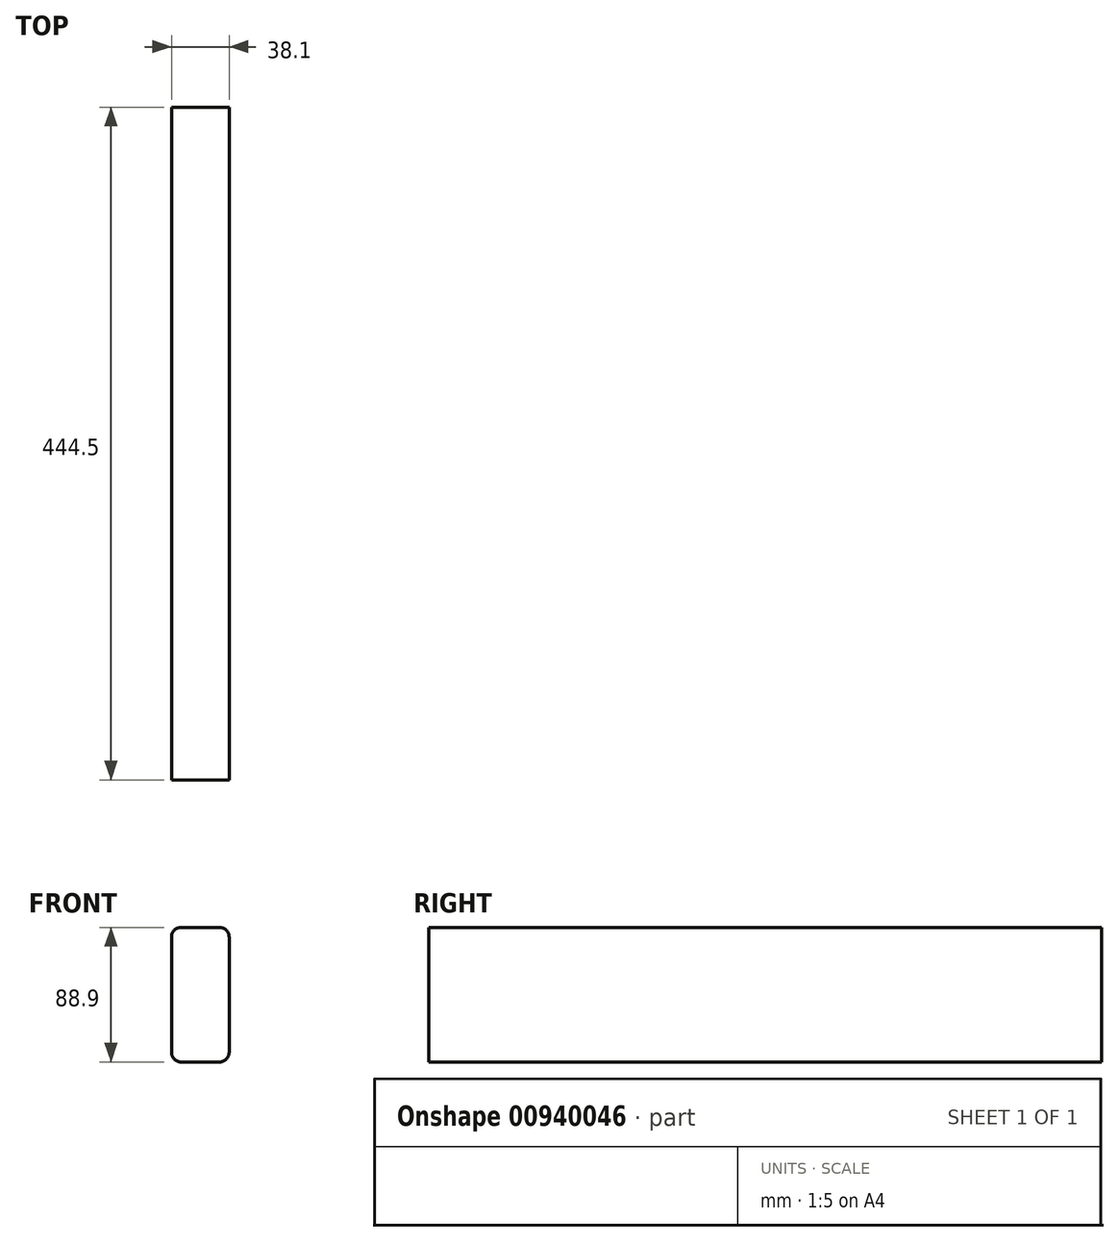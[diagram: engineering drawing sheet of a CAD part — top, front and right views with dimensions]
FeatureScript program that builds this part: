
annotation { "Feature Type Name" : "Feature", "Feature Type Description" : "" }
export const myFeature = defineFeature(function(context is Context, id is Id, definition is map)
    precondition{}
    {
        {
            var Q0;
            Q0=qCreatedBy(makeId("Front.planeOp"),FACE);
            var sketch = newSketch(context, id + "F0", { "sketchPlane" : qUnion([Q0])});
            skLineSegment(sketch, "E0.bottom", {"start": v(12.7, 44.45) * mm, "end": v(-12.7, 44.45) * mm});
            skLineSegment(sketch, "E0.top", {"start": v(12.7, -44.45) * mm, "end": v(-12.7, -44.45) * mm});
            skLineSegment(sketch, "E0.left", {"start": v(19.05, 38.1) * mm, "end": v(19.05, -38.1) * mm});
            skLineSegment(sketch, "E0.right", {"start": v(-19.05, 38.1) * mm, "end": v(-19.05, -38.1) * mm});
            skPoint(sketch, "E0.middle", {"position": v(0, 0) * mm});
            skPoint(sketch, "E1.visualSharp", {"position": v(-19.05, 44.45) * mm});
            skArc(sketch, "E1.filletArc", {"start": v(-12.7, 44.45) * mm, "mid": v(-17.2, 42.6) * mm, "end": v(-19.05, 38.1) * mm});
            skPoint(sketch, "E2.visualSharp", {"position": v(19.05, 44.45) * mm});
            skArc(sketch, "E2.filletArc", {"start": v(19.05, 38.1) * mm, "mid": v(17.2, 42.6) * mm, "end": v(12.7, 44.45) * mm});
            skPoint(sketch, "E3.visualSharp", {"position": v(19.05, -44.45) * mm});
            skArc(sketch, "E3.filletArc", {"start": v(12.7, -44.45) * mm, "mid": v(17.2, -42.6) * mm, "end": v(19.05, -38.1) * mm});
            skPoint(sketch, "E4.visualSharp", {"position": v(-19.05, -44.45) * mm});
            skArc(sketch, "E4.filletArc", {"start": v(-19.05, -38.1) * mm, "mid": v(-17.2, -42.6) * mm, "end": v(-12.7, -44.45) * mm});
            skSolve(sketch);
        }
        {
            var Q0;
            Q0 = qSketchRegion(id + "F0", true);
            extrude(context, id + "F1", {"entities" : qUnion([Q0]), "depth" : 444.5 * mm, "offsetDistance" : 25.4 * mm});
        }
    });
